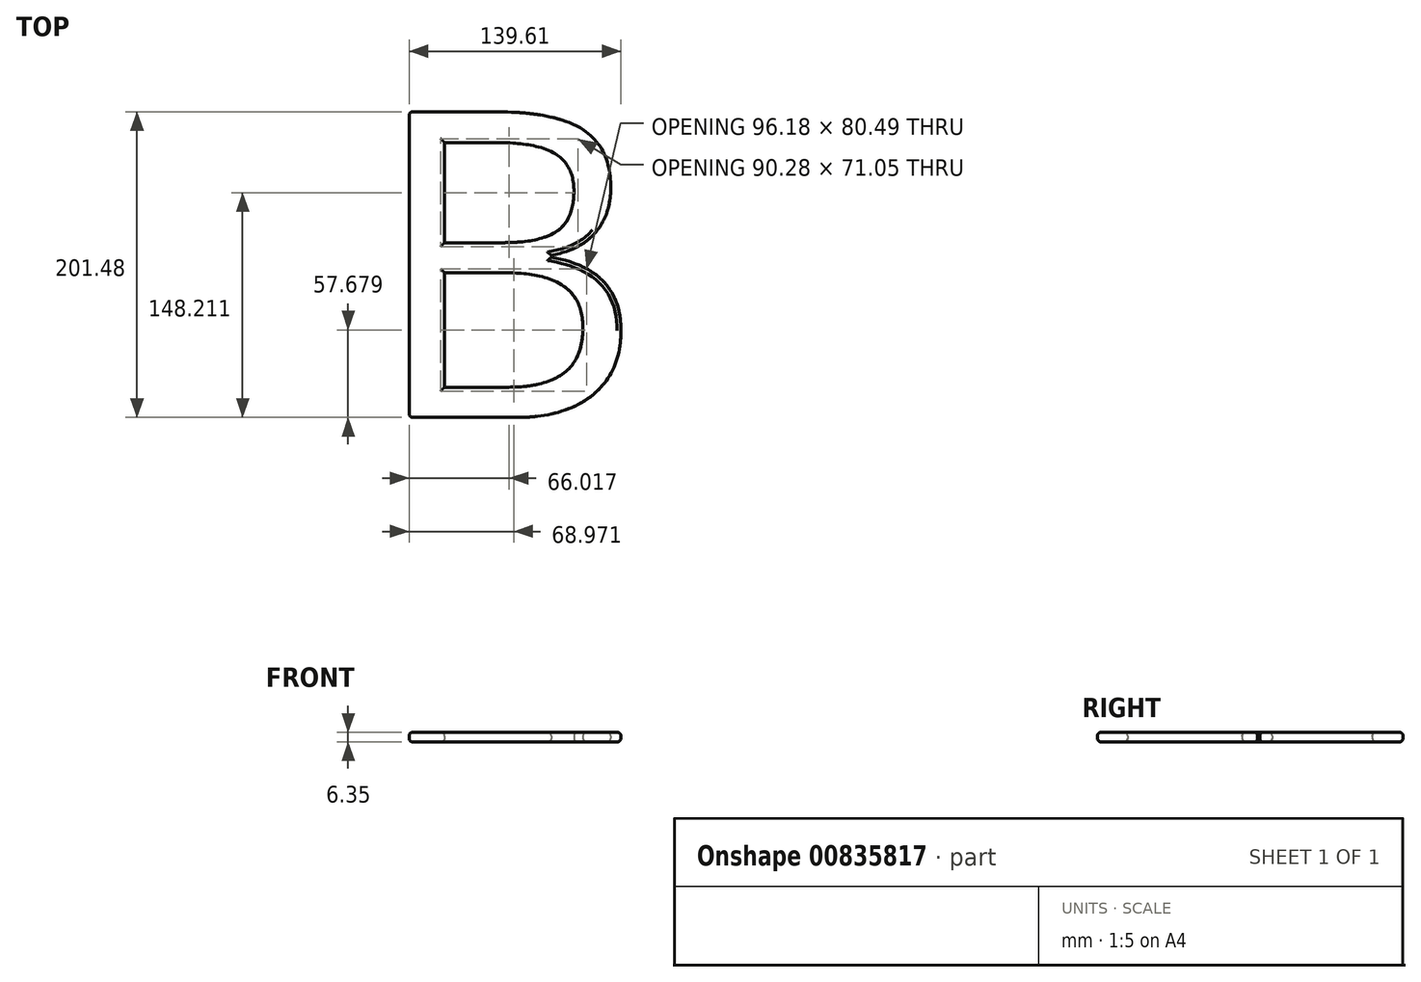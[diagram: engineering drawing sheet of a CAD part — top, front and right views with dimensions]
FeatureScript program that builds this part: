
annotation { "Feature Type Name" : "Feature", "Feature Type Description" : "" }
export const myFeature = defineFeature(function(context is Context, id is Id, definition is map)
    precondition{}
    {
        {
            var Q0;
            Q0=qCreatedBy(makeId("Top.planeOp"),FACE);
            var sketch = newSketch(context, id + "F0", { "sketchPlane" : qUnion([Q0])});
            skText(sketch, "E0", { "text": "B", "fontName": "OpenSans-Regular.ttf"});
            const initialGuessF0  = {"E0": [0, -0.2032, 1, 0, 0.2032]};
            skSetInitialGuess(sketch, initialGuessF0);
            skSolve(sketch);
        }
        {
            var Q0;
            Q0=makeQuery(id+"F0.imprint","IMPRINT",FACE,{"disambiguationData":[TD([[makeQuery(id+"F0.imprint","IMPRINT",EDGE,{"derivedFrom":sQuery(id+"F0.wireOp",EDGE,"E0.sketch_text.stroke-0")}),-1.0]])]});
            extrude(context, id + "F1", {"entities" : qUnion([Q0]), "depth" : 6.35 * mm, "offsetDistance" : 25.4 * mm});
        }
        {
            var Q0;
            Q0=makeQuery(id+"F1.opExtrude","CAP_FACE",FACE,{"disambiguationData":[OSD([sQuery(id+"F0.wireOp",EDGE,"E0.sketch_text.stroke-0"),sQuery(id+"F0.wireOp",EDGE,"E0.sketch_text.stroke-1"),sQuery(id+"F0.wireOp",EDGE,"E0.sketch_text.stroke-2"),sQuery(id+"F0.wireOp",EDGE,"E0.sketch_text.stroke-3"),sQuery(id+"F0.wireOp",EDGE,"E0.sketch_text.stroke-4"),sQuery(id+"F0.wireOp",EDGE,"E0.sketch_text.stroke-5"),sQuery(id+"F0.wireOp",EDGE,"E0.sketch_text.stroke-6"),sQuery(id+"F0.wireOp",EDGE,"E0.sketch_text.stroke-7"),sQuery(id+"F0.wireOp",EDGE,"E0.sketch_text.stroke-8"),sQuery(id+"F0.wireOp",EDGE,"E0.sketch_text.stroke-9"),sQuery(id+"F0.wireOp",EDGE,"E0.sketch_text.stroke-10"),sQuery(id+"F0.wireOp",EDGE,"E0.sketch_text.stroke-11"),sQuery(id+"F0.wireOp",EDGE,"E0.sketch_text.stroke-12"),sQuery(id+"F0.wireOp",EDGE,"E0.sketch_text.stroke-13"),sQuery(id+"F0.wireOp",EDGE,"E0.sketch_text.stroke-14"),sQuery(id+"F0.wireOp",EDGE,"E0.sketch_text.stroke-15"),sQuery(id+"F0.wireOp",EDGE,"E0.sketch_text.stroke-16"),sQuery(id+"F0.wireOp",EDGE,"E0.sketch_text.stroke-17"),sQuery(id+"F0.wireOp",EDGE,"E0.sketch_text.stroke-18"),sQuery(id+"F0.wireOp",EDGE,"E0.sketch_text.stroke-19"),sQuery(id+"F0.wireOp",EDGE,"E0.sketch_text.stroke-20"),sQuery(id+"F0.wireOp",EDGE,"E0.sketch_text.stroke-21"),sQuery(id+"F0.wireOp",EDGE,"E0.sketch_text.stroke-22"),sQuery(id+"F0.wireOp",EDGE,"E0.sketch_text.stroke-23"),sQuery(id+"F0.wireOp",EDGE,"E0.sketch_text.stroke-24")])],"isStart":false});
            var Q1;
            Q1=makeQuery(id+"F1.opExtrude","CAP_FACE",FACE,{"disambiguationData":[OSD([sQuery(id+"F0.wireOp",EDGE,"E0.sketch_text.stroke-0"),sQuery(id+"F0.wireOp",EDGE,"E0.sketch_text.stroke-1"),sQuery(id+"F0.wireOp",EDGE,"E0.sketch_text.stroke-2"),sQuery(id+"F0.wireOp",EDGE,"E0.sketch_text.stroke-3"),sQuery(id+"F0.wireOp",EDGE,"E0.sketch_text.stroke-4"),sQuery(id+"F0.wireOp",EDGE,"E0.sketch_text.stroke-5"),sQuery(id+"F0.wireOp",EDGE,"E0.sketch_text.stroke-6"),sQuery(id+"F0.wireOp",EDGE,"E0.sketch_text.stroke-7"),sQuery(id+"F0.wireOp",EDGE,"E0.sketch_text.stroke-8"),sQuery(id+"F0.wireOp",EDGE,"E0.sketch_text.stroke-9"),sQuery(id+"F0.wireOp",EDGE,"E0.sketch_text.stroke-10"),sQuery(id+"F0.wireOp",EDGE,"E0.sketch_text.stroke-11"),sQuery(id+"F0.wireOp",EDGE,"E0.sketch_text.stroke-12"),sQuery(id+"F0.wireOp",EDGE,"E0.sketch_text.stroke-13"),sQuery(id+"F0.wireOp",EDGE,"E0.sketch_text.stroke-14"),sQuery(id+"F0.wireOp",EDGE,"E0.sketch_text.stroke-15"),sQuery(id+"F0.wireOp",EDGE,"E0.sketch_text.stroke-16"),sQuery(id+"F0.wireOp",EDGE,"E0.sketch_text.stroke-17"),sQuery(id+"F0.wireOp",EDGE,"E0.sketch_text.stroke-18"),sQuery(id+"F0.wireOp",EDGE,"E0.sketch_text.stroke-19"),sQuery(id+"F0.wireOp",EDGE,"E0.sketch_text.stroke-20"),sQuery(id+"F0.wireOp",EDGE,"E0.sketch_text.stroke-21"),sQuery(id+"F0.wireOp",EDGE,"E0.sketch_text.stroke-22"),sQuery(id+"F0.wireOp",EDGE,"E0.sketch_text.stroke-23"),sQuery(id+"F0.wireOp",EDGE,"E0.sketch_text.stroke-24")])],"isStart":true});
            fillet(context, id + "F2", {"entities" : qUnion([Q0, Q1]), "radius" : 2.54 * mm, "tangentPropagation" : true, "allowEdgeOverflow" : false});
        }
        {
            var Q0;
            Q0=makeQuery(id+"F2.opFillet","BLEND_EDGE",EDGE,{"blendedFrom":[makeQuery(id+"F1.opExtrude","CAP_EDGE",EDGE,{"disambiguationData":[OSD([sQuery(id+"F0.wireOp",EDGE,"E0.sketch_text.stroke-9")])],"isStart":false}),makeQuery(id+"F1.opExtrude","CAP_EDGE",EDGE,{"disambiguationData":[OSD([sQuery(id+"F0.wireOp",EDGE,"E0.sketch_text.stroke-10")])],"isStart":false})],"blendedInto":[]});
            var Q1;
            Q1=makeQuery(id+"F2.opFillet","BLEND_EDGE",EDGE,{"blendedFrom":[makeQuery(id+"F1.opExtrude","CAP_EDGE",EDGE,{"disambiguationData":[OSD([sQuery(id+"F0.wireOp",EDGE,"E0.sketch_text.stroke-9")])],"isStart":true}),makeQuery(id+"F1.opExtrude","CAP_EDGE",EDGE,{"disambiguationData":[OSD([sQuery(id+"F0.wireOp",EDGE,"E0.sketch_text.stroke-10")])],"isStart":true})],"blendedInto":[]});
            var Q2;
            Q2=makeQuery(id+"F1.opExtrude","SWEPT_EDGE",EDGE,{"disambiguationData":[OSD([sQuery(id+"F0.wireOp",EDGE,"E0.sketch_text.stroke-9"),sQuery(id+"F0.wireOp",EDGE,"E0.sketch_text.stroke-10")])]});
            var Q3;
            Q3=makeQuery(id+"F2.opFillet","BLEND_EDGE",EDGE,{"blendedFrom":[makeQuery(id+"F1.opExtrude","CAP_EDGE",EDGE,{"disambiguationData":[OSD([sQuery(id+"F0.wireOp",EDGE,"E0.sketch_text.stroke-0")])],"isStart":true}),makeQuery(id+"F1.opExtrude","CAP_EDGE",EDGE,{"disambiguationData":[OSD([sQuery(id+"F0.wireOp",EDGE,"E0.sketch_text.stroke-10")])],"isStart":true})],"blendedInto":[]});
            var Q4;
            Q4=makeQuery(id+"F2.opFillet","BLEND_EDGE",EDGE,{"blendedFrom":[makeQuery(id+"F1.opExtrude","CAP_EDGE",EDGE,{"disambiguationData":[OSD([sQuery(id+"F0.wireOp",EDGE,"E0.sketch_text.stroke-0")])],"isStart":false}),makeQuery(id+"F1.opExtrude","CAP_EDGE",EDGE,{"disambiguationData":[OSD([sQuery(id+"F0.wireOp",EDGE,"E0.sketch_text.stroke-10")])],"isStart":false})],"blendedInto":[]});
            var Q5;
            Q5=makeQuery(id+"F1.opExtrude","SWEPT_EDGE",EDGE,{"disambiguationData":[OSD([sQuery(id+"F0.wireOp",EDGE,"E0.sketch_text.stroke-0"),sQuery(id+"F0.wireOp",EDGE,"E0.sketch_text.stroke-10")])]});
            fillet(context, id + "F3", {"entities" : qUnion([Q0, Q1, Q2, Q3, Q4, Q5]), "radius" : 2.54 * mm, "tangentPropagation" : true, "allowEdgeOverflow" : false});
        }
    });
